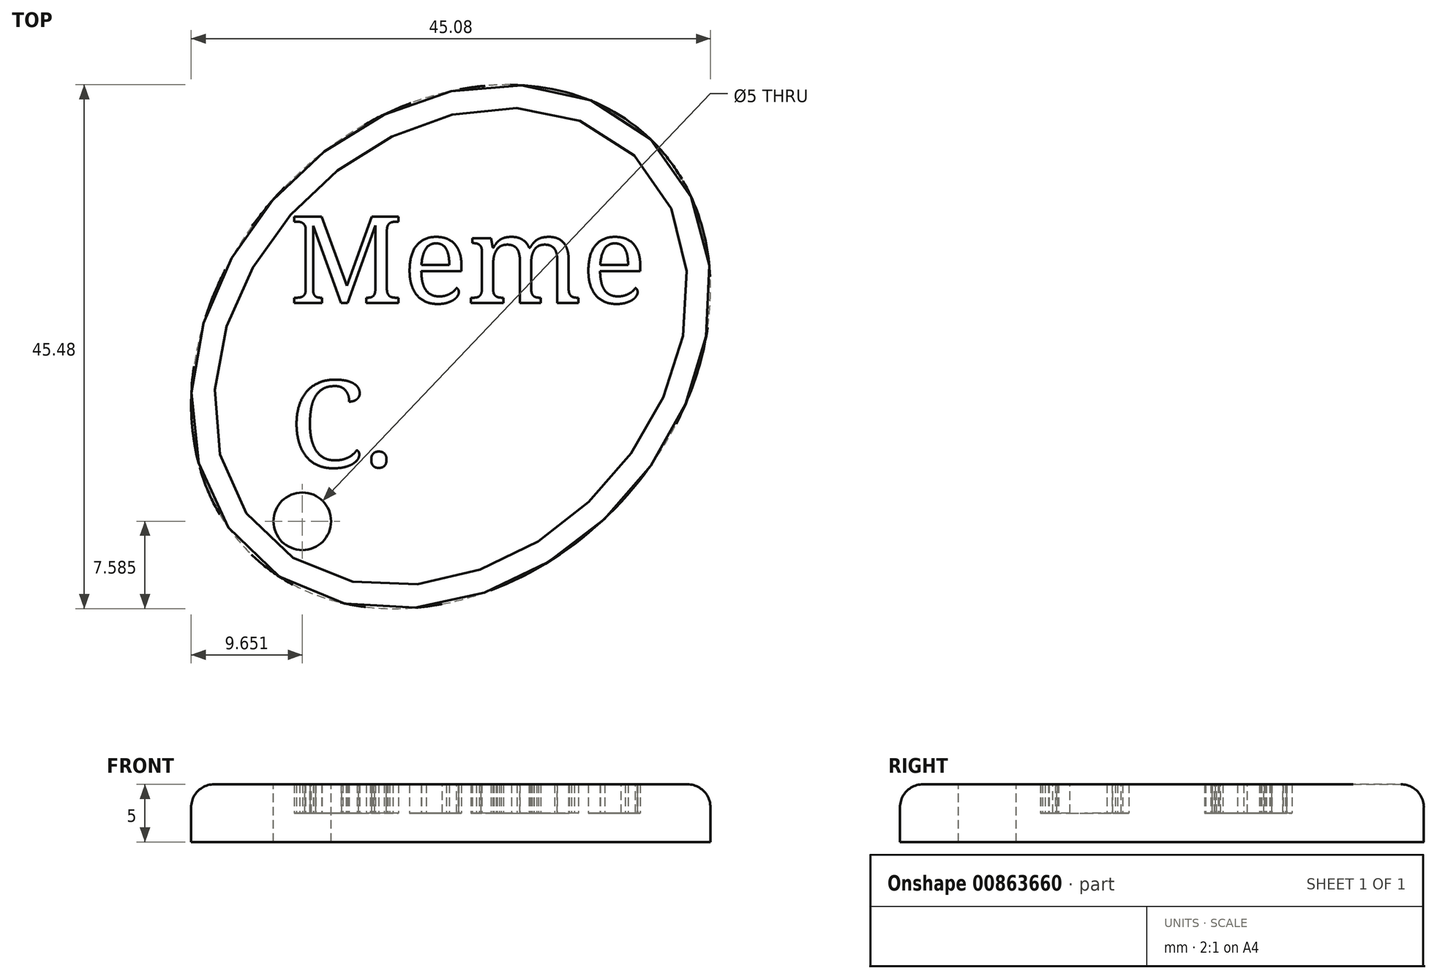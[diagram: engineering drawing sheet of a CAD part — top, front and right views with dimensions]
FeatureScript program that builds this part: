
annotation { "Feature Type Name" : "Feature", "Feature Type Description" : "" }
export const myFeature = defineFeature(function(context is Context, id is Id, definition is map)
    precondition{}
    {
        {
            var Q0;
            Q0=qCreatedBy(makeId("Top.planeOp"),FACE);
            var sketch = newSketch(context, id + "F0", { "sketchPlane" : qUnion([Q0])});
            skEllipse(sketch, "E0", {"center": v(0, 0) * mm, "majorRadius": 25 * mm, "minorRadius": 20 * mm, "majorAxis": v(0.7, 0.72)});
            skPoint(sketch, "E1", {"position": v(-13.06, -15.82) * mm});
            skSolve(sketch);
        }
        {
            var Q0;
            Q0=makeQuery(id+"F0.imprint","IMPRINT",FACE,{"disambiguationData":[TD([[makeQuery(id+"F0.imprint","IMPRINT",EDGE,{"derivedFrom":sQuery(id+"F0.wireOp",EDGE,"E0")}),1.0]])]});
            extrude(context, id + "F1", {"entities" : qUnion([Q0]), "depth" : 5 * mm, "offsetDistance" : 25 * mm});
        }
        {
            var Q0;
            Q0=makeQuery(id+"F1.opExtrude","CAP_FACE",FACE,{"disambiguationData":[OSD([sQuery(id+"F0.wireOp",EDGE,"E0")])],"isStart":false});
            var sketch = newSketch(context, id + "F2", { "sketchPlane" : qUnion([Q0])});
            skPoint(sketch, "E2", {"position": v(-12.89, -15.16) * mm});
            skSolve(sketch);
        }
        {
            var Q0;
            Q0=sQuery(id+"F2.wireOp",VERTEX,"E2");
            var Q1;
            Q1=makeQuery(id+"F1.opExtrude","SWEPT_BODY",BODY,{"disambiguationData":[OSD([sQuery(id+"F0.wireOp",EDGE,"E0")])]});
            hole(context, id + "F3", {"style" : HoleStyle.SIMPLE, "endStyle" : HoleEndStyle.THROUGH, "holeDiameter" : 5 * mm, "majorDiameter" : 5 * mm, "isTappedThrough" : true, "tappedDepth" : 12 * mm, "tapClearance" : 3, "locations" : qUnion([Q0]), "scope" : qUnion([Q1])});
        }
        {
            var Q0;
            Q0=makeQuery(id+"F1.opExtrude","CAP_EDGE",EDGE,{"disambiguationData":[OSD([sQuery(id+"F0.wireOp",EDGE,"E0")])],"isStart":false});
            fillet(context, id + "F4", {"entities" : qUnion([Q0]), "radius" : 2 * mm, "tangentPropagation" : true, "allowEdgeOverflow" : false});
        }
        {
            var Q0;
            Q0=makeQuery(id+"F1.opExtrude","CAP_FACE",FACE,{"disambiguationData":[OSD([sQuery(id+"F0.wireOp",EDGE,"E0")])],"isStart":false});
            var sketch = newSketch(context, id + "F5", { "sketchPlane" : qUnion([Q0])});
            skText(sketch, "E3", { "text": "Meme\nC.", "fontName": "NotoSerif-Regular.ttf"});
            const initialGuessF5  = {"E3": [-0.01399, 0.00381, 1, 0, 0.00755]};
            skSetInitialGuess(sketch, initialGuessF5);
            skSolve(sketch);
        }
        {
            var Q0;
            Q0 = qSketchRegion(id + "F5", true);
            extrude(context, id + "F6", {"entities" : qUnion([Q0]), "operationType" : NewBodyOperationType.REMOVE, "endBound" : BoundingType.SYMMETRIC, "depth" : 5 * mm, "offsetDistance" : 25 * mm});
        }
    });
